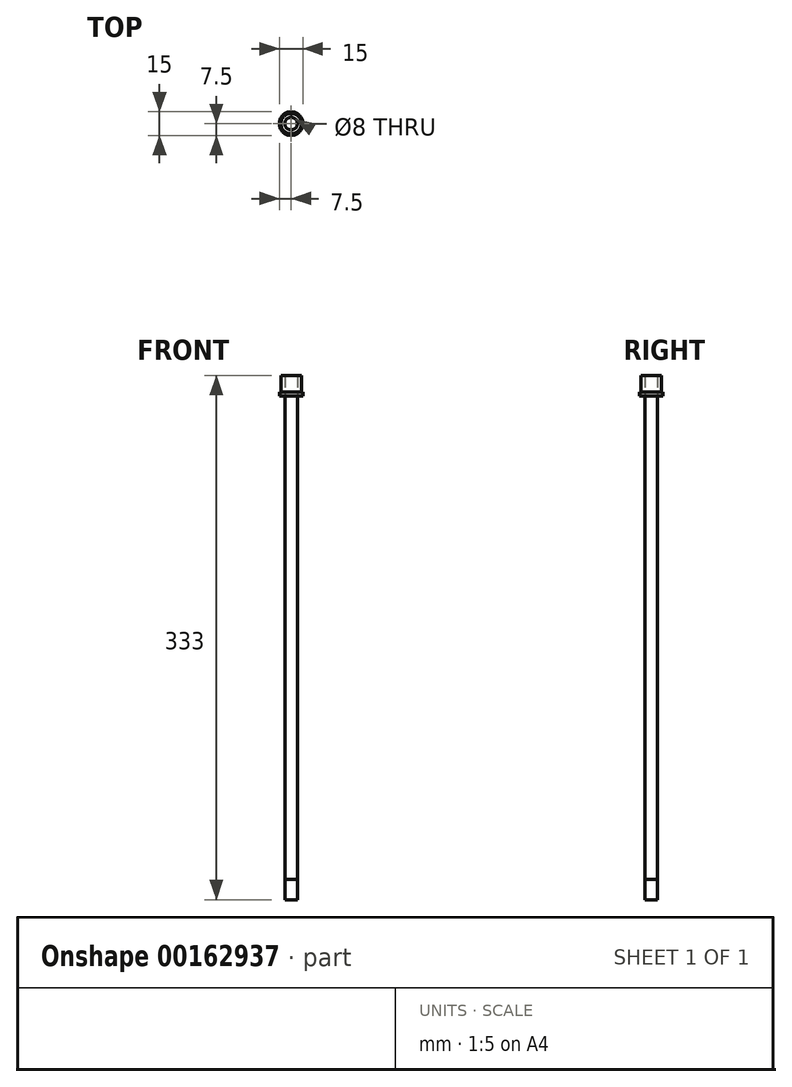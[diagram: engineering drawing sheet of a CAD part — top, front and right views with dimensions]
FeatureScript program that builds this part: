
annotation { "Feature Type Name" : "Feature", "Feature Type Description" : "" }
export const myFeature = defineFeature(function(context is Context, id is Id, definition is map)
    precondition{}
    {
        {
            var Q0;
            Q0=qCreatedBy(makeId("Top.planeOp"),FACE);
            var sketch = newSketch(context, id + "F0", { "sketchPlane" : qUnion([Q0])});
            skCircle(sketch, "E0", {"center": v(0, 0) * mm, "radius": 6.5 * mm});
            skCircle(sketch, "E1", {"center": v(0, 0) * mm, "radius": 7.5 * mm});
            skCircle(sketch, "E2", {"center": v(0, 0) * mm, "radius": 4 * mm});
            skSolve(sketch);
        }
        {
            var Q0;
            Q0 = qSketchRegion(id + "F0", true);
            var Q1;
            Q1=makeQuery(id+"F0.imprint","IMPRINT",FACE,{"disambiguationData":[TD([[makeQuery(id+"F0.imprint","IMPRINT",EDGE,{"derivedFrom":sQuery(id+"F0.wireOp",EDGE,"E0")}),1.0]])]});
            var Q2;
            Q2=makeQuery(id+"F0.imprint","IMPRINT",FACE,{"disambiguationData":[TD([[makeQuery(id+"F0.imprint","IMPRINT",EDGE,{"derivedFrom":sQuery(id+"F0.wireOp",EDGE,"E2")}),1.0]])]});
            extrude(context, id + "F1", {"entities" : qUnion([Q0, Q1, Q2]), "depth" : 2.5 * mm});
        }
        {
            var Q0;
            Q0=makeQuery(id+"F0.imprint","IMPRINT",FACE,{"disambiguationData":[TD([[makeQuery(id+"F0.imprint","IMPRINT",EDGE,{"derivedFrom":sQuery(id+"F0.wireOp",EDGE,"E2")}),1.0]])]});
            extrude(context, id + "F2", {"entities" : qUnion([Q0]), "oppositeDirection" : true, "depth" : 320 * mm});
        }
        {
            var Q0;
            Q0=makeQuery(id+"F0.imprint","IMPRINT",FACE,{"disambiguationData":[TD([[makeQuery(id+"F0.imprint","IMPRINT",EDGE,{"derivedFrom":sQuery(id+"F0.wireOp",EDGE,"E0")}),1.0]])]});
            var Q1;
            Q1=makeQuery(id+"F2.opExtrude","CAP_FACE",FACE,{"disambiguationData":[OSD([sQuery(id+"F0.wireOp",EDGE,"E2")])],"isStart":false});
            extrude(context, id + "F3", {"entities" : qUnion([Q0, Q1]), "depth" : 13 * mm});
        }
    });
